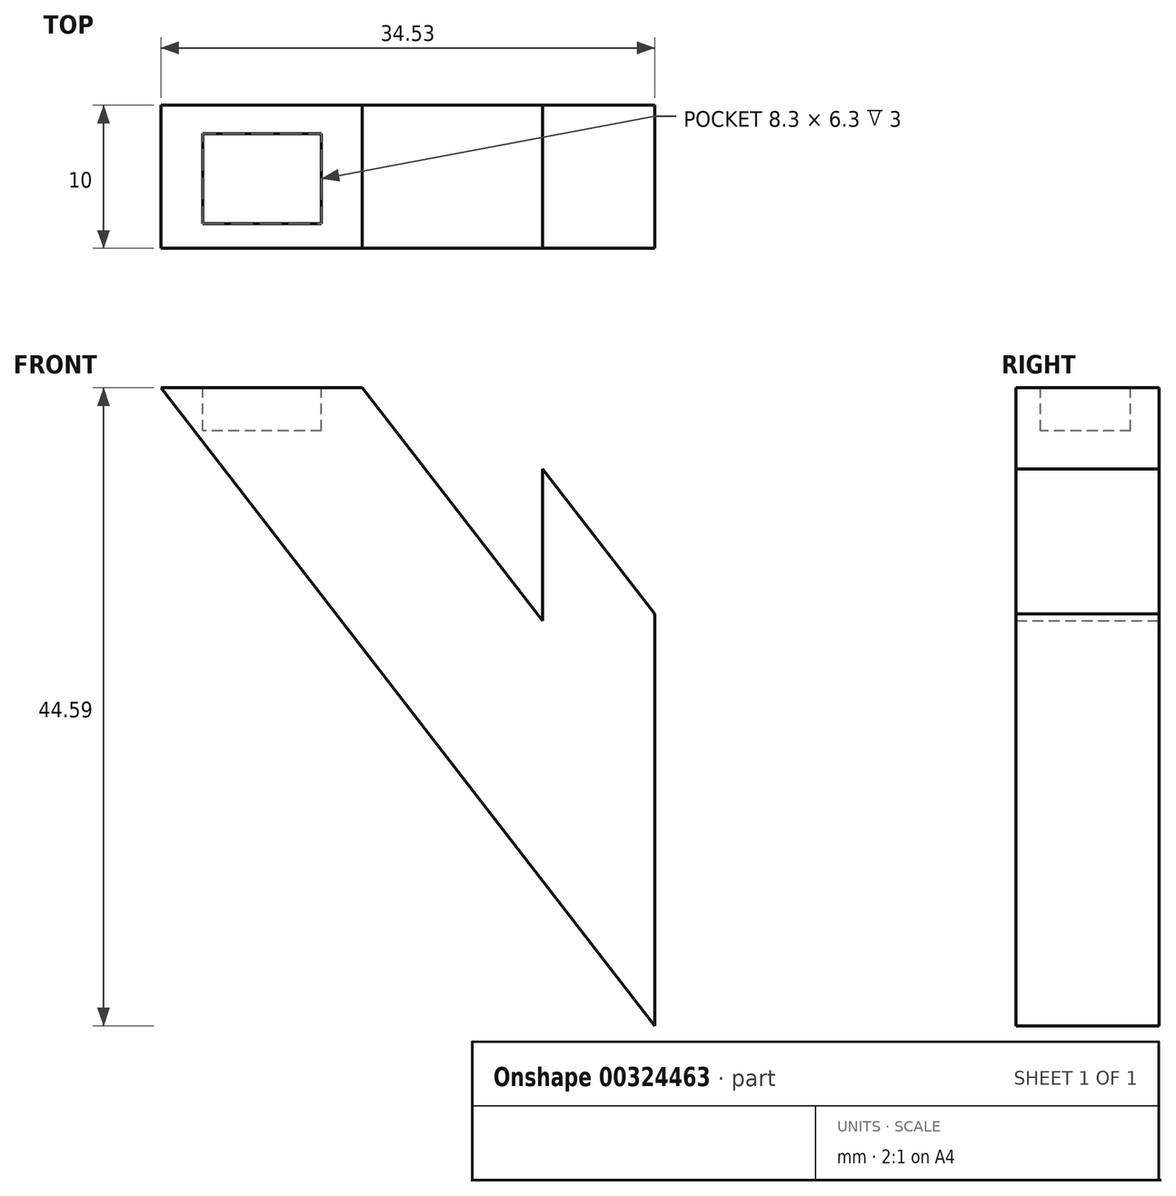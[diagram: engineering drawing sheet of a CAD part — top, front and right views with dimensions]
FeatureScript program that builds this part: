
annotation { "Feature Type Name" : "Feature", "Feature Type Description" : "" }
export const myFeature = defineFeature(function(context is Context, id is Id, definition is map)
    precondition{}
    {
        {
            var Q0;
            Q0=qCreatedBy(makeId("Front.planeOp"),FACE);
            var sketch = newSketch(context, id + "F0", { "sketchPlane" : qUnion([Q0])});
            skLineSegment(sketch, "E0", {"start": v(0, 0) * mm, "end": v(34.53, -44.6) * mm});
            skLineSegment(sketch, "E1", {"start": v(34.53, -44.6) * mm, "end": v(34.53, -15.8) * mm});
            skLineSegment(sketch, "E2", {"start": v(34.53, -15.8) * mm, "end": v(26.7, -5.67) * mm});
            skLineSegment(sketch, "E3", {"start": v(26.7, -5.67) * mm, "end": v(26.7, -16.27) * mm});
            skLineSegment(sketch, "E4", {"start": v(26.7, -16.27) * mm, "end": v(14.1, 0) * mm});
            skLineSegment(sketch, "E5", {"start": v(14.1, 0) * mm, "end": v(0, 0) * mm});
            skSolve(sketch);
        }
        {
            var Q0;
            Q0=makeQuery(id+"F0.imprint","IMPRINT",FACE,{"disambiguationData":[TD([[makeQuery(id+"F0.imprint","IMPRINT",EDGE,{"derivedFrom":sQuery(id+"F0.wireOp",EDGE,"E0")}),1.0]])]});
            extrude(context, id + "F1", {"entities" : qUnion([Q0]), "depth" : 10 * mm});
        }
        {
            var Q0;
            Q0=qCreatedBy(makeId("Top.planeOp"),FACE);
            var sketch = newSketch(context, id + "F2", { "sketchPlane" : qUnion([Q0])});
            skLineSegment(sketch, "E6.bottom", {"start": v(11.23, -1.99) * mm, "end": v(2.93, -1.99) * mm});
            skLineSegment(sketch, "E6.top", {"start": v(11.23, -8.29) * mm, "end": v(2.93, -8.29) * mm});
            skLineSegment(sketch, "E6.left", {"start": v(11.23, -1.99) * mm, "end": v(11.23, -8.29) * mm});
            skLineSegment(sketch, "E6.right", {"start": v(2.93, -1.99) * mm, "end": v(2.93, -8.29) * mm});
            skPoint(sketch, "E6.middle", {"position": v(7.08, -5.14) * mm});
            skSolve(sketch);
        }
        {
            var Q0;
            Q0 = qSketchRegion(id + "F2", true);
            extrude(context, id + "F3", {"entities" : qUnion([Q0]), "operationType" : NewBodyOperationType.REMOVE, "oppositeDirection" : true, "depth" : 3 * mm});
        }
    });
